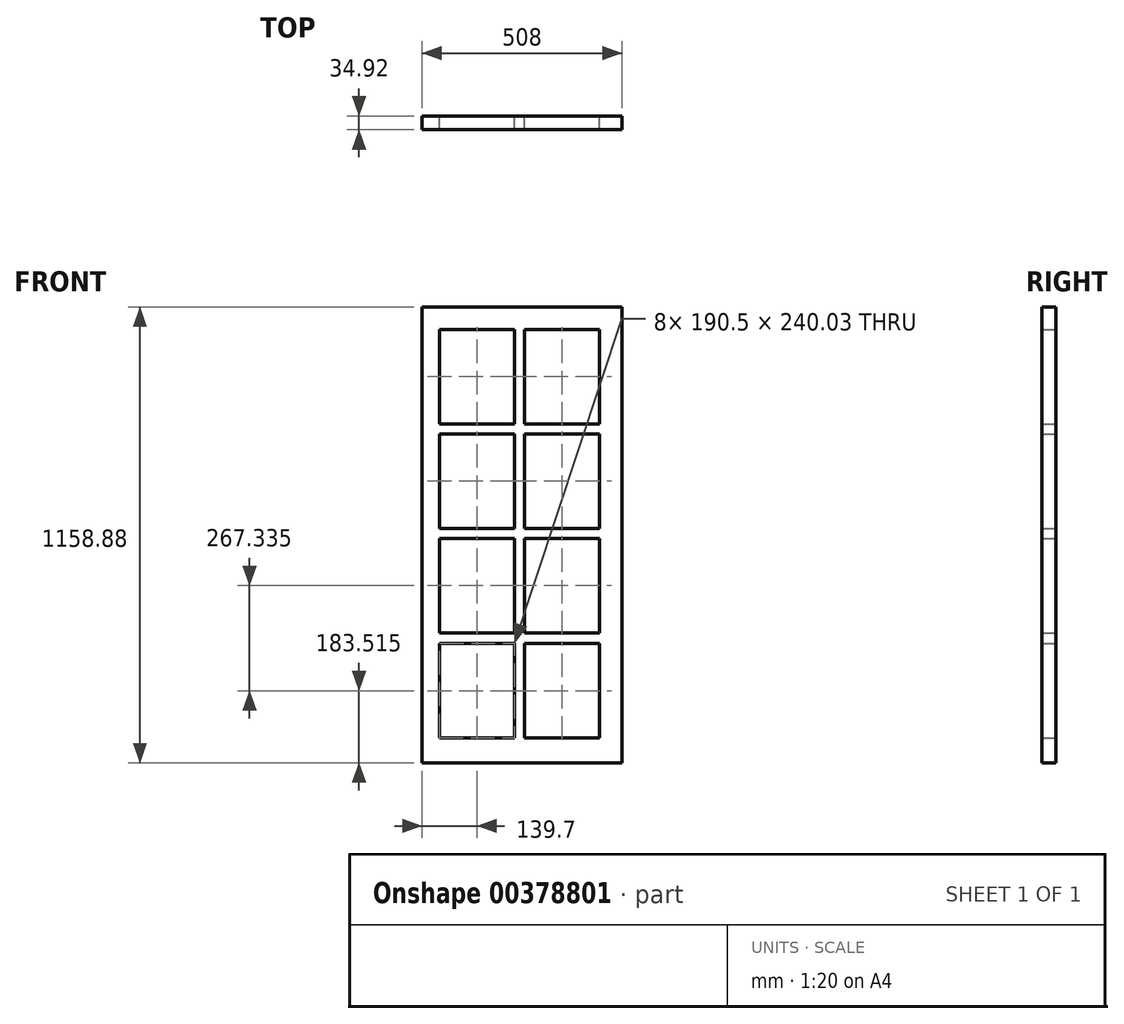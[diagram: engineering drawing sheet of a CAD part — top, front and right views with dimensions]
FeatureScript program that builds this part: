
annotation { "Feature Type Name" : "Feature", "Feature Type Description" : "" }
export const myFeature = defineFeature(function(context is Context, id is Id, definition is map)
    precondition{}
    {
        {
            var Q0;
            Q0=qCreatedBy(makeId("Front.planeOp"),FACE);
            var sketch = newSketch(context, id + "F0", { "sketchPlane" : qUnion([Q0])});
            skLineSegment(sketch, "E0.bottom", {"start": v(0, 0) * mm, "end": v(508, 0) * mm});
            skLineSegment(sketch, "E0.top", {"start": v(0, 1158.88) * mm, "end": v(508, 1158.88) * mm});
            skLineSegment(sketch, "E0.left", {"start": v(0, 0) * mm, "end": v(0, 1158.87) * mm});
            skLineSegment(sketch, "E0.right", {"start": v(508, 0) * mm, "end": v(508, 1158.88) * mm});
            skLineSegment(sketch, "E1.bottom", {"start": v(44.45, 1101.73) * mm, "end": v(234.95, 1101.73) * mm});
            skLineSegment(sketch, "E1.top", {"start": v(44.45, 861.7) * mm, "end": v(234.95, 861.7) * mm});
            skLineSegment(sketch, "E1.left", {"start": v(44.45, 1101.73) * mm, "end": v(44.45, 861.7) * mm});
            skLineSegment(sketch, "E1.right", {"start": v(234.95, 1101.73) * mm, "end": v(234.95, 861.7) * mm});
            skLineSegment(sketch, "E2.bottom", {"start": v(44.45, 63.5) * mm, "end": v(234.95, 63.5) * mm});
            skLineSegment(sketch, "E2.top", {"start": v(44.45, 303.53) * mm, "end": v(234.95, 303.53) * mm});
            skLineSegment(sketch, "E2.left", {"start": v(44.45, 63.5) * mm, "end": v(44.45, 303.53) * mm});
            skLineSegment(sketch, "E2.right", {"start": v(234.95, 63.5) * mm, "end": v(234.95, 303.53) * mm});
            skLineSegment(sketch, "E3.bottom", {"start": v(44.45, 330.84) * mm, "end": v(234.95, 330.84) * mm});
            skLineSegment(sketch, "E3.top", {"start": v(44.45, 570.87) * mm, "end": v(234.95, 570.87) * mm});
            skLineSegment(sketch, "E3.left", {"start": v(44.45, 330.84) * mm, "end": v(44.45, 570.87) * mm});
            skLineSegment(sketch, "E3.right", {"start": v(234.95, 330.84) * mm, "end": v(234.95, 570.87) * mm});
            skLineSegment(sketch, "E4.bottom", {"start": v(44.45, 596.27) * mm, "end": v(234.95, 596.27) * mm});
            skLineSegment(sketch, "E4.top", {"start": v(44.45, 836.3) * mm, "end": v(234.95, 836.3) * mm});
            skLineSegment(sketch, "E4.left", {"start": v(44.45, 596.27) * mm, "end": v(44.45, 836.3) * mm});
            skLineSegment(sketch, "E4.right", {"start": v(234.95, 596.27) * mm, "end": v(234.95, 836.3) * mm});
            skLineSegment(sketch, "E5.bottom", {"start": v(260.35, 1101.73) * mm, "end": v(450.85, 1101.73) * mm});
            skLineSegment(sketch, "E5.top", {"start": v(260.35, 861.7) * mm, "end": v(450.85, 861.7) * mm});
            skLineSegment(sketch, "E5.left", {"start": v(260.35, 1101.73) * mm, "end": v(260.35, 861.7) * mm});
            skLineSegment(sketch, "E5.right", {"start": v(450.85, 1101.73) * mm, "end": v(450.85, 861.7) * mm});
            skLineSegment(sketch, "E6.bottom", {"start": v(260.35, 836.3) * mm, "end": v(450.85, 836.3) * mm});
            skLineSegment(sketch, "E6.top", {"start": v(260.35, 596.27) * mm, "end": v(450.85, 596.27) * mm});
            skLineSegment(sketch, "E6.left", {"start": v(260.35, 836.3) * mm, "end": v(260.35, 596.27) * mm});
            skLineSegment(sketch, "E6.right", {"start": v(450.85, 836.3) * mm, "end": v(450.85, 596.27) * mm});
            skLineSegment(sketch, "E7.bottom", {"start": v(260.35, 570.87) * mm, "end": v(450.85, 570.87) * mm});
            skLineSegment(sketch, "E7.top", {"start": v(260.35, 330.84) * mm, "end": v(450.85, 330.84) * mm});
            skLineSegment(sketch, "E7.left", {"start": v(260.35, 570.87) * mm, "end": v(260.35, 330.84) * mm});
            skLineSegment(sketch, "E7.right", {"start": v(450.85, 570.87) * mm, "end": v(450.85, 330.84) * mm});
            skLineSegment(sketch, "E8.bottom", {"start": v(260.35, 303.53) * mm, "end": v(450.85, 303.53) * mm});
            skLineSegment(sketch, "E8.top", {"start": v(260.35, 63.5) * mm, "end": v(450.85, 63.5) * mm});
            skLineSegment(sketch, "E8.left", {"start": v(260.35, 303.53) * mm, "end": v(260.35, 63.5) * mm});
            skLineSegment(sketch, "E8.right", {"start": v(450.85, 303.53) * mm, "end": v(450.85, 63.5) * mm});
            skSolve(sketch);
        }
        {
            var Q0;
            Q0=makeQuery(id+"F0.imprint","IMPRINT",FACE,{"disambiguationData":[TD([[makeQuery(id+"F0.imprint","IMPRINT",EDGE,{"derivedFrom":sQuery(id+"F0.wireOp",EDGE,"E0.bottom")}),1.0]])]});
            extrude(context, id + "F1", {"entities" : qUnion([Q0]), "depth" : 34.92 * mm});
        }
    });
